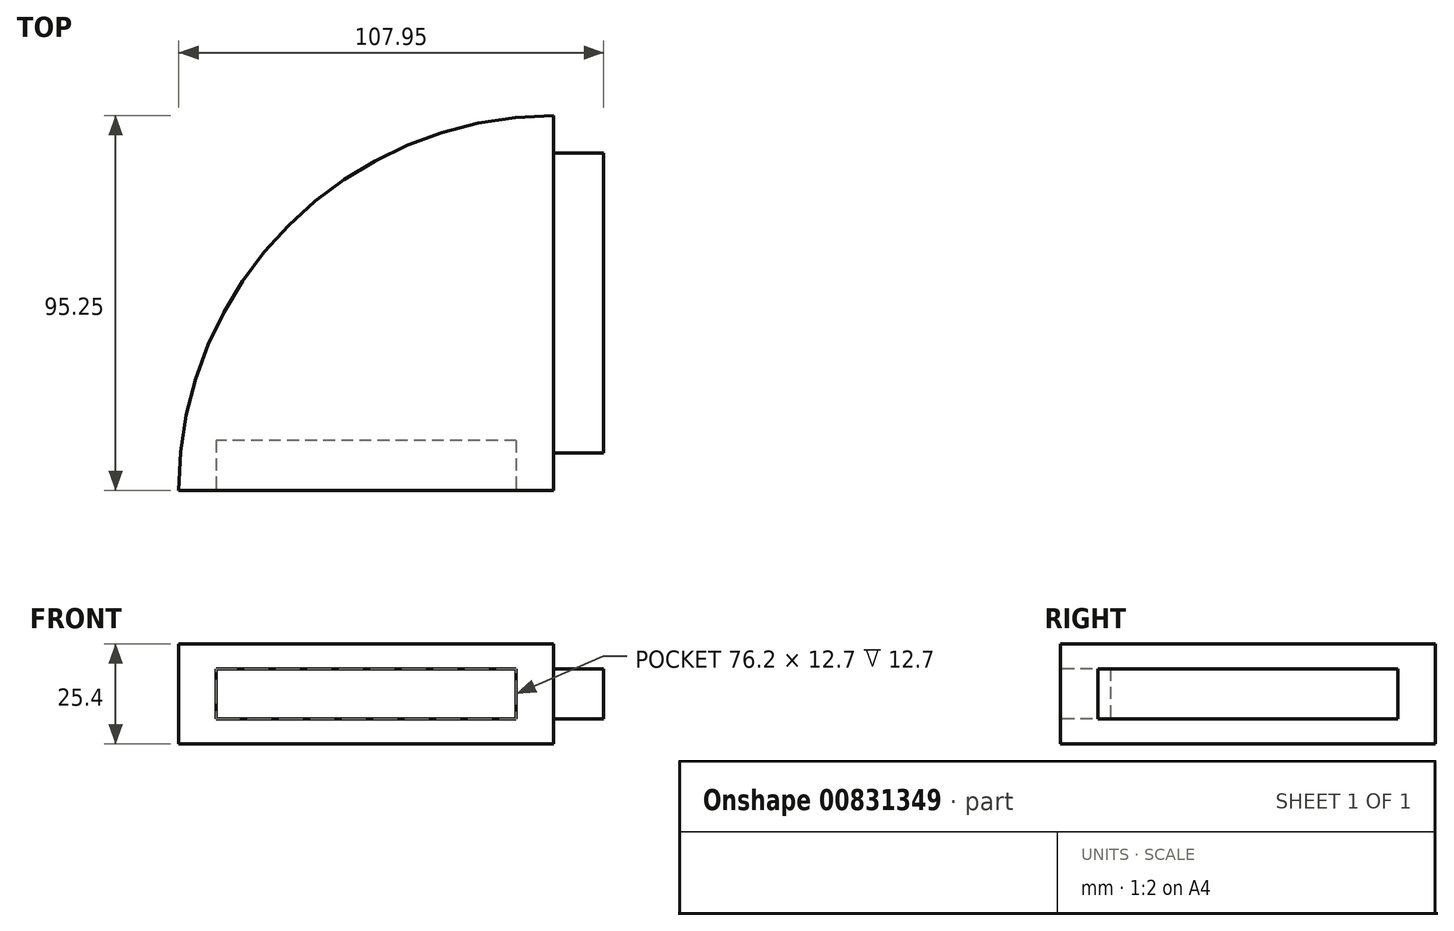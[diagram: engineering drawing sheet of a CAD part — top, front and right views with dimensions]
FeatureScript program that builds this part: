
annotation { "Feature Type Name" : "Feature", "Feature Type Description" : "" }
export const myFeature = defineFeature(function(context is Context, id is Id, definition is map)
    precondition{}
    {
        {
            var Q0;
            Q0=qCreatedBy(makeId("Top.planeOp"),FACE);
            var sketch = newSketch(context, id + "F0", { "sketchPlane" : qUnion([Q0])});
            skLineSegment(sketch, "E0", {"start": v(0, 0) * mm, "end": v(0, 95.25) * mm});
            skLineSegment(sketch, "E1", {"start": v(0, 0) * mm, "end": v(-95.25, 0) * mm});
            skArc(sketch, "E2", {"start": v(-95.25, 0) * mm, "mid": v(-67.35, 67.35) * mm, "end": v(0, 95.25) * mm});
            skSolve(sketch);
        }
        {
            var Q0;
            Q0 = qSketchRegion(id + "F0", true);
            extrude(context, id + "F1", {"entities" : qUnion([Q0]), "oppositeDirection" : true, "depth" : 25.4 * mm, "offsetDistance" : 25.4 * mm});
        }
        {
            var Q0;
            Q0=makeQuery(id+"F1.opExtrude","SWEPT_FACE",FACE,{"disambiguationData":[OSD([sQuery(id+"F0.wireOp",EDGE,"E1")])]});
            var sketch = newSketch(context, id + "F2", { "sketchPlane" : qUnion([Q0])});
            skLineSegment(sketch, "E3", {"start": v(-47.62, -25.4) * mm, "end": v(-47.62, -19.05) * mm, "construction": true});
            skLineSegment(sketch, "E4", {"start": v(-47.62, 0) * mm, "end": v(-47.62, -6.35) * mm, "construction": true});
            skLineSegment(sketch, "E5.right", {"start": v(-9.53, -6.35) * mm, "end": v(-9.53, -19.05) * mm});
            skLineSegment(sketch, "E6", {"start": v(-9.52, -6.35) * mm, "end": v(-85.72, -6.35) * mm});
            skLineSegment(sketch, "E7", {"start": v(-85.72, -19.05) * mm, "end": v(-85.72, -6.35) * mm});
            skLineSegment(sketch, "E8", {"start": v(-95.25, -12.7) * mm, "end": v(-85.72, -12.7) * mm, "construction": true});
            skLineSegment(sketch, "E9", {"start": v(0, -12.7) * mm, "end": v(-9.53, -12.7) * mm, "construction": true});
            skLineSegment(sketch, "E10", {"start": v(-9.52, -19.05) * mm, "end": v(-85.72, -19.05) * mm});
            skSolve(sketch);
        }
        {
            var Q0;
            Q0 = qSketchRegion(id + "F2", true);
            extrude(context, id + "F3", {"entities" : qUnion([Q0]), "operationType" : NewBodyOperationType.REMOVE, "oppositeDirection" : true, "depth" : 12.7 * mm, "offsetDistance" : 25.4 * mm});
        }
        {
            var Q0;
            Q0=makeQuery(id+"F1.opExtrude","SWEPT_FACE",FACE,{"disambiguationData":[OSD([sQuery(id+"F0.wireOp",EDGE,"E0")])]});
            var sketch = newSketch(context, id + "F4", { "sketchPlane" : qUnion([Q0])});
            skLineSegment(sketch, "E11", {"start": v(47.62, -25.4) * mm, "end": v(47.62, -19.05) * mm, "construction": true});
            skLineSegment(sketch, "E12", {"start": v(47.62, 0) * mm, "end": v(47.62, -6.35) * mm, "construction": true});
            skLineSegment(sketch, "E13", {"start": v(0, -12.7) * mm, "end": v(9.53, -12.7) * mm, "construction": true});
            skLineSegment(sketch, "E14", {"start": v(95.25, -12.7) * mm, "end": v(85.72, -12.7) * mm, "construction": true});
            skLineSegment(sketch, "E15", {"start": v(9.53, -12.7) * mm, "end": v(9.52, -19.05) * mm});
            skLineSegment(sketch, "E16", {"start": v(47.62, -19.05) * mm, "end": v(9.52, -19.05) * mm});
            skLineSegment(sketch, "E17", {"start": v(47.62, -19.05) * mm, "end": v(85.72, -19.05) * mm});
            skLineSegment(sketch, "E18", {"start": v(85.72, -12.7) * mm, "end": v(85.72, -19.05) * mm});
            skLineSegment(sketch, "E19", {"start": v(85.72, -12.7) * mm, "end": v(85.72, -6.35) * mm});
            skLineSegment(sketch, "E20", {"start": v(9.53, -12.7) * mm, "end": v(9.53, -6.35) * mm});
            skLineSegment(sketch, "E21", {"start": v(47.62, -6.35) * mm, "end": v(9.53, -6.35) * mm});
            skLineSegment(sketch, "E22", {"start": v(47.62, -6.35) * mm, "end": v(85.72, -6.35) * mm});
            skSolve(sketch);
        }
        {
            var Q0;
            Q0 = qSketchRegion(id + "F4", true);
            extrude(context, id + "F5", {"entities" : qUnion([Q0]), "operationType" : NewBodyOperationType.ADD, "depth" : 12.7 * mm, "offsetDistance" : 25.4 * mm});
        }
    });
